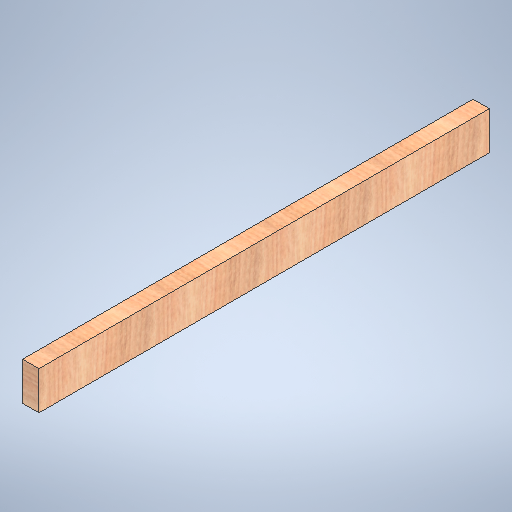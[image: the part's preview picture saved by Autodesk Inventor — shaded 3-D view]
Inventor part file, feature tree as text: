
AUTODESK INVENTOR PART (.ipt)
format: ipt  version: 2025.1 (Build 291241020, 241B)  size: 338,944 bytes
history: native  units: in
note: dims shown in document units (in); Inventor stores cm internally (conversion verified against a paired STEP export)
features: extrude x1, sketch x1
ambient origin geometry x8: Origin, YZ Plane, XZ Plane, XY Plane, X Axis, Y Axis, Z Axis, Center Point
bodies: Solid1 (feature_tree)
feature tree (2):
  extrude  "Extrusion1"  Depth=1.5in TaperAngle=0.0deg
  sketch  "Sketch1"  dims[d1=41.25in d2=1.5in d3=0.0in d4=3.5in]
